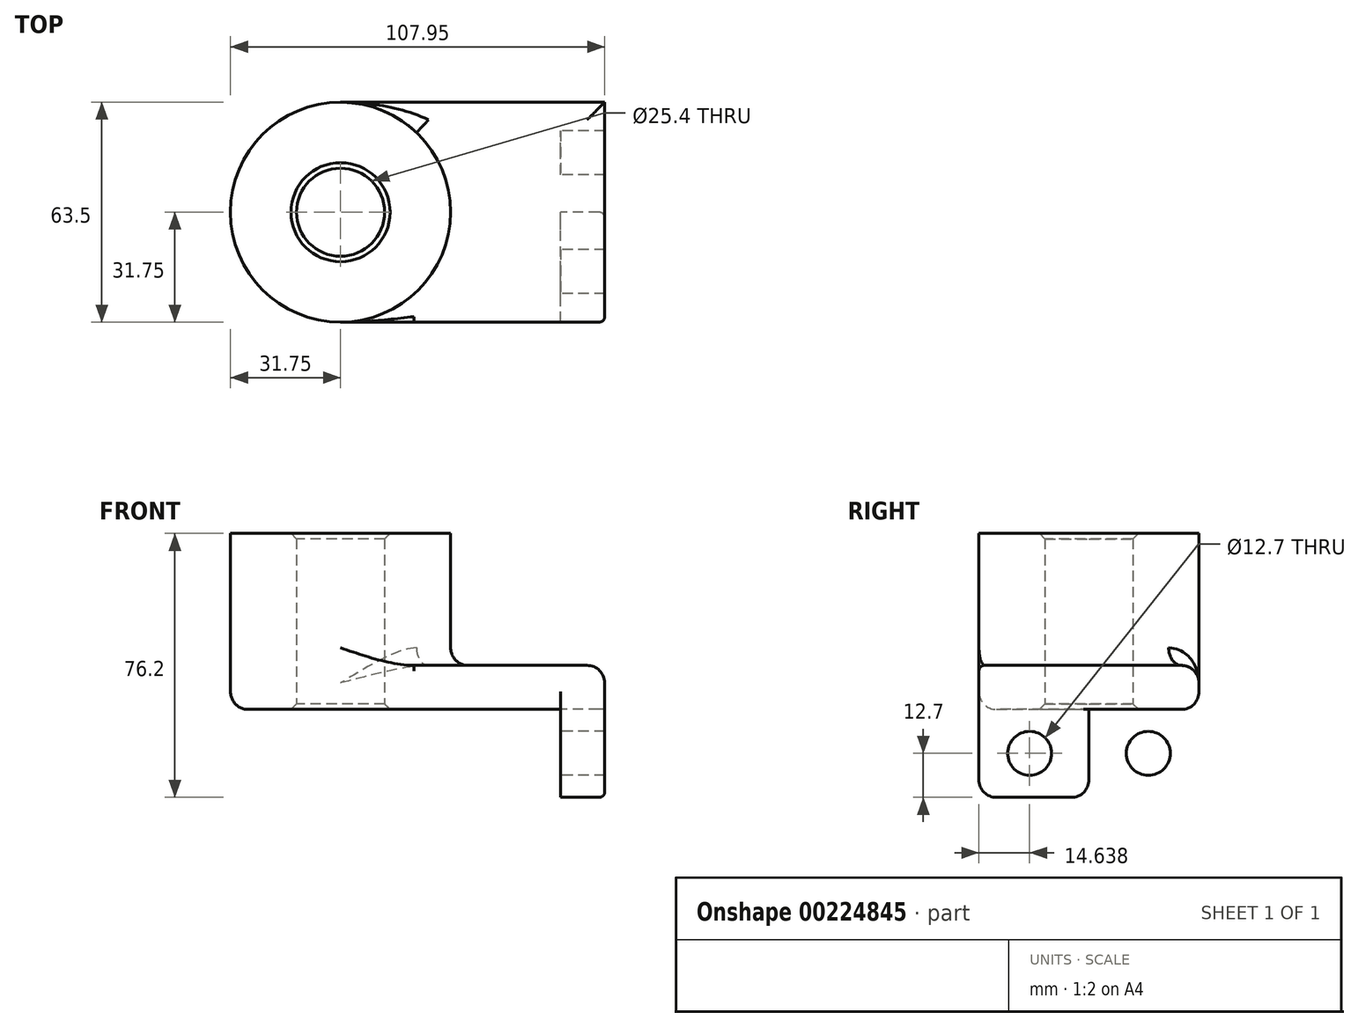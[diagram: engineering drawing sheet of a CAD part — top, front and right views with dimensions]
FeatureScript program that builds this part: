
annotation { "Feature Type Name" : "Feature", "Feature Type Description" : "" }
export const myFeature = defineFeature(function(context is Context, id is Id, definition is map)
    precondition{}
    {
        {
            var Q0;
            Q0=qCreatedBy(makeId("Top.planeOp"),FACE);
            var sketch = newSketch(context, id + "F0", { "sketchPlane" : qUnion([Q0])});
            skLineSegment(sketch, "E0.bottom", {"start": v(31.75, -31.75) * mm, "end": v(-31.75, -31.75) * mm});
            skLineSegment(sketch, "E0.top", {"start": v(31.75, 31.75) * mm, "end": v(-31.75, 31.75) * mm});
            skLineSegment(sketch, "E0.left", {"start": v(31.75, -31.75) * mm, "end": v(31.75, 31.75) * mm});
            skLineSegment(sketch, "E0.right", {"start": v(-31.75, -31.75) * mm, "end": v(-31.75, 31.75) * mm});
            skPoint(sketch, "E0.middle", {"position": v(0, 0) * mm});
            skCircle(sketch, "E1", {"center": v(-31.75, 0) * mm, "radius": 31.75 * mm});
            skCircle(sketch, "E2", {"center": v(-31.75, 0) * mm, "radius": 12.7 * mm});
            skSolve(sketch);
        }
        {
            var Q0;
            Q0 = qSketchRegion(id + "F0", true);
            extrude(context, id + "F1", {"entities" : qUnion([Q0]), "depth" : 12.7 * mm});
        }
        {
            var Q0;
            {var subQ1=sQuery(id+"F0.wireOp",EDGE,"E0.right");var subQ3=sQuery(id+"F0.wireOp",EDGE,"E2");var subQ4=makeQuery(id+"F0.imprint","INTERSECT",VERTEX,{"disambiguationData":[OD(0.0)],"derivedFrom":[subQ1,subQ3]});Q0=makeQuery(id+"F0.imprint","IMPRINT",FACE,{"disambiguationData":[TD([[makeQuery(id+"F0.imprint","IMPRINT",EDGE,{"disambiguationData":[TD([[subQ4,-1.0]])],"derivedFrom":subQ3}),-1.0]])]});}
            var Q1;
            {var subQ1=sQuery(id+"F0.wireOp",EDGE,"E0.right");var subQ3=sQuery(id+"F0.wireOp",EDGE,"E2");var subQ4=makeQuery(id+"F0.imprint","INTERSECT",VERTEX,{"disambiguationData":[OD(0.0)],"derivedFrom":[subQ1,subQ3]});Q1=makeQuery(id+"F0.imprint","IMPRINT",FACE,{"disambiguationData":[TD([[makeQuery(id+"F0.imprint","IMPRINT",EDGE,{"disambiguationData":[TD([[subQ4,1.0]])],"derivedFrom":subQ3}),-1.0]])]});}
            extrude(context, id + "F2", {"entities" : qUnion([Q0, Q1]), "operationType" : NewBodyOperationType.ADD, "depth" : 50.8 * mm});
        }
        {
            var Q0;
            Q0=makeQuery(id+"F1.opExtrude","SWEPT_FACE",FACE,{"disambiguationData":[OSD([sQuery(id+"F0.wireOp",EDGE,"E0.left")])]});
            var sketch = newSketch(context, id + "F3", { "sketchPlane" : qUnion([Q0])});
            skLineSegment(sketch, "E3.bottom", {"start": v(-31.75, 12.7) * mm, "end": v(31.75, 12.7) * mm});
            skLineSegment(sketch, "E3.top", {"start": v(-31.75, -25.4) * mm, "end": v(31.75, -25.4) * mm});
            skLineSegment(sketch, "E3.left", {"start": v(-31.75, 12.7) * mm, "end": v(-31.75, -25.4) * mm});
            skLineSegment(sketch, "E3.right", {"start": v(31.75, 12.7) * mm, "end": v(31.75, -25.4) * mm});
            skLineSegment(sketch, "E4", {"start": v(0, 12.7) * mm, "end": v(0, -25.4) * mm});
            skCircle(sketch, "E5", {"center": v(-17.11, -12.7) * mm, "radius": 6.35 * mm});
            skCircle(sketch, "E6.MirrorC", {"center": v(17.11, -12.7) * mm, "radius": 6.35 * mm});
            skSolve(sketch);
        }
        {
            var Q0;
            {var subQ0=sQuery(id+"F3.wireOp",EDGE,"E3.left");var subQ1=sQuery(id+"F3.wireOp",EDGE,"E3.bottom");var subQ2=makeQuery(id+"F3.imprint","INTERSECT",VERTEX,{"derivedFrom":[subQ1,subQ0]});Q0=makeQuery(id+"F3.imprint","IMPRINT",FACE,{"disambiguationData":[TD([[makeQuery(id+"F3.imprint","IMPRINT",EDGE,{"disambiguationData":[TD([[subQ2,-1.0]])],"derivedFrom":subQ1}),-1.0]])]});}
            var Q1;
            {var subQ0=sQuery(id+"F3.wireOp",EDGE,"E3.right");var subQ1=sQuery(id+"F3.wireOp",EDGE,"E3.bottom");var subQ2=makeQuery(id+"F3.imprint","INTERSECT",VERTEX,{"derivedFrom":[subQ1,subQ0]});Q1=makeQuery(id+"F3.imprint","IMPRINT",FACE,{"disambiguationData":[TD([[makeQuery(id+"F3.imprint","IMPRINT",EDGE,{"disambiguationData":[TD([[subQ2,1.0]])],"derivedFrom":subQ1}),-1.0]])]});}
            var Q2;
            Q2=makeQuery(id+"F3.imprint","IMPRINT",FACE,{"disambiguationData":[TD([[makeQuery(id+"F3.imprint","IMPRINT",EDGE,{"derivedFrom":sQuery(id+"F3.wireOp",EDGE,"E5")}),-1.0]])]});
            var Q3;
            Q3=makeQuery(id+"F3.imprint","IMPRINT",FACE,{"disambiguationData":[TD([[makeQuery(id+"F3.imprint","IMPRINT",EDGE,{"derivedFrom":sQuery(id+"F3.wireOp",EDGE,"E6.MirrorC")}),1.0]])]});
            extrude(context, id + "F4", {"entities" : qUnion([Q0, Q1, Q2, Q3]), "operationType" : NewBodyOperationType.ADD, "depth" : 12.7 * mm});
        }
        {
            var Q0;
            {var subQ0=sQuery(id+"F0.wireOp",EDGE,"E1");Q0=makeQuery(id+"F2.boolean.opBoolean","INTERSECT",EDGE,{"derivedFrom":[makeQuery(id+"F1.opExtrude","CAP_FACE",FACE,{"disambiguationData":[OSD([sQuery(id+"F0.wireOp",EDGE,"E0.bottom"),sQuery(id+"F0.wireOp",EDGE,"E0.top"),sQuery(id+"F0.wireOp",EDGE,"E0.left"),subQ0,sQuery(id+"F0.wireOp",EDGE,"E2")])],"isStart":false}),makeQuery(id+"F2.opExtrude","SWEPT_FACE",FACE,{"disambiguationData":[OSD([subQ0])]})]});}
            var Q1;
            Q1=makeQuery(id+"F4.opExtrude","CAP_EDGE",EDGE,{"disambiguationData":[OSD([sQuery(id+"F3.wireOp",EDGE,"E3.bottom")])],"isStart":false});
            var Q2;
            Q2=makeQuery(id+"F4.opExtrude","SWEPT_EDGE",EDGE,{"disambiguationData":[OSD([sQuery(id+"F3.wireOp",EDGE,"E3.top"),sQuery(id+"F3.wireOp",EDGE,"E3.left")])]});
            var Q3;
            Q3=makeQuery(id+"F4.opExtrude","SWEPT_EDGE",EDGE,{"disambiguationData":[OSD([sQuery(id+"F3.wireOp",EDGE,"E3.top"),sQuery(id+"F3.wireOp",EDGE,"E3.right")])]});
            fillet(context, id + "F5", {"entities" : qUnion([Q0, Q1, Q2, Q3]), "radius" : 5.08 * mm, "tangentPropagation" : true, "allowEdgeOverflow" : false});
        }
        {
            var Q0;
            Q0=makeQuery(id+"F1.opExtrude","CAP_EDGE",EDGE,{"disambiguationData":[OSD([sQuery(id+"F0.wireOp",EDGE,"E0.bottom")])],"isStart":true});
            var Q1;
            Q1=makeQuery(id+"F4.boolean.opBoolean","MERGE",EDGE,{"derivedFrom":[makeQuery(id+"F1.opExtrude","CAP_EDGE",EDGE,{"disambiguationData":[OSD([sQuery(id+"F0.wireOp",EDGE,"E0.bottom")])],"isStart":false}),makeQuery(id+"F4.opExtrude","SWEPT_EDGE",EDGE,{"disambiguationData":[OSD([sQuery(id+"F3.wireOp",EDGE,"E3.bottom"),sQuery(id+"F3.wireOp",EDGE,"E3.left")])]})]});
            var Q2;
            Q2=makeQuery(id+"F1.opExtrude","CAP_EDGE",EDGE,{"disambiguationData":[OSD([sQuery(id+"F0.wireOp",EDGE,"E0.left")])],"isStart":true});
            fillet(context, id + "F6", {"entities" : qUnion([Q0, Q1, Q2]), "radius" : 1.59 * mm, "tangentPropagation" : true, "allowEdgeOverflow" : false});
        }
        {
            var Q0;
            {var subQ0=sQuery(id+"F0.wireOp",EDGE,"E2");Q0=makeQuery(id+"F2.boolean.opBoolean","MERGE",FACE,{"derivedFrom":[makeQuery(id+"F1.opExtrude","SWEPT_FACE",FACE,{"disambiguationData":[OSD([subQ0])]}),makeQuery(id+"F2.opExtrude","SWEPT_FACE",FACE,{"disambiguationData":[OSD([subQ0])]})]});}
            chamfer(context, id + "F7", {"entities" : qUnion([Q0]), "width" : 1.59 * mm, "tangentPropagation" : true});
        }
    });
